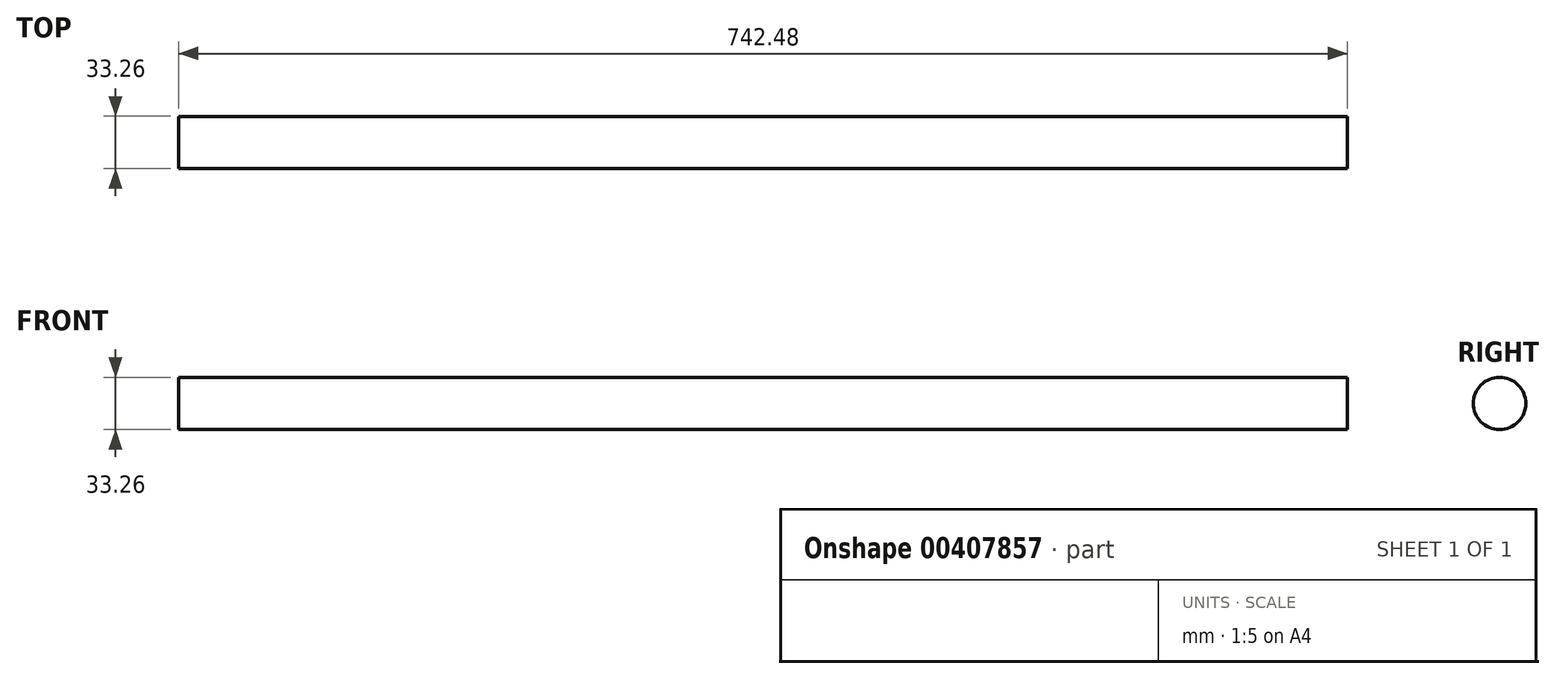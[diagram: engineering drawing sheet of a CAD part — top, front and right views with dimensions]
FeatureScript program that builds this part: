
annotation { "Feature Type Name" : "Feature", "Feature Type Description" : "" }
export const myFeature = defineFeature(function(context is Context, id is Id, definition is map)
    precondition{}
    {
        {
            var Q0;
            Q0=qCreatedBy(makeId("Right.planeOp"),FACE);
            var sketch = newSketch(context, id + "F0", { "sketchPlane" : qUnion([Q0])});
            skCircle(sketch, "E0", {"center": v(0, 0) * mm, "radius": 16.63 * mm});
            skSolve(sketch);
        }
        {
            var Q0;
            Q0 = qBodyType(qCreatedBy(id + "F0" ,EDGE), BodyType.WIRE);
            var sketch = newSketch(context, id + "F1", { "sketchPlane" : qUnion([Q0])});
            skSolve(sketch);
        }
        {
            var Q0;
            Q0 = qSketchRegion(id + "F1", true);
            var Q1;
            Q1=makeQuery(id+"F0.imprint","IMPRINT",FACE,{"disambiguationData":[TD([[makeQuery(id+"F0.imprint","IMPRINT",EDGE,{"derivedFrom":sQuery(id+"F0.wireOp",EDGE,"E0")}),1.0]])]});
            extrude(context, id + "F2", {"entities" : qUnion([Q0, Q1]), "depth" : 742.48 * mm});
        }
    });
